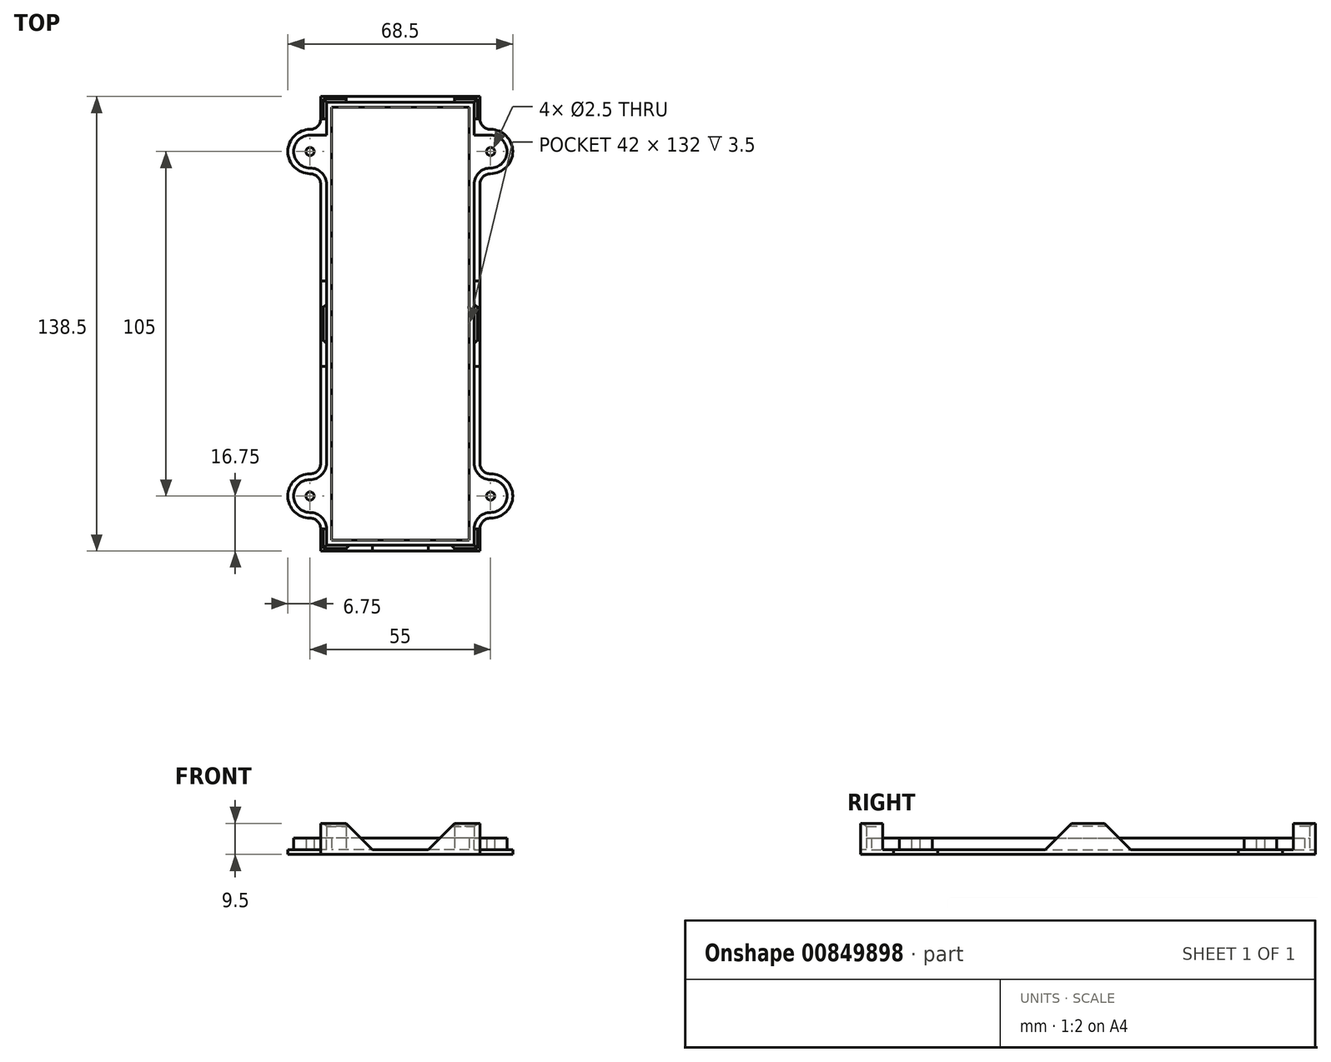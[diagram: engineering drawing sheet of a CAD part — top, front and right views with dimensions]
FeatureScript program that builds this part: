
annotation { "Feature Type Name" : "Feature", "Feature Type Description" : "" }
export const myFeature = defineFeature(function(context is Context, id is Id, definition is map)
    precondition{}
    {
        {
            var Q0;
            Q0=qCreatedBy(makeId("Top.planeOp"),FACE);
            var sketch = newSketch(context, id + "F0", { "sketchPlane" : qUnion([Q0])});
            skLineSegment(sketch, "E0.bottom", {"start": v(0, 0) * mm, "end": v(-45, 0) * mm});
            skLineSegment(sketch, "E0.top", {"start": v(0, 135) * mm, "end": v(-45, 135) * mm});
            skLineSegment(sketch, "E0.left", {"start": v(0, 0) * mm, "end": v(0, 135) * mm});
            skLineSegment(sketch, "E0.right", {"start": v(-45, 0) * mm, "end": v(-45, 135) * mm});
            skSolve(sketch);
        }
        {
            var Q0;
            Q0=qSketchRegion(id+"F0",true);
            extrude(context, id + "F1", {"entities" : qUnion([Q0]), "depth" : 40 * mm, "offsetDistance" : 25 * mm});
        }
        {
            var Q0;
            Q0=makeQuery(id+"F1.opExtrude","CAP_FACE",FACE,{"disambiguationData":[OSD([sQuery(id+"F0.wireOp",EDGE,"E0.bottom"),sQuery(id+"F0.wireOp",EDGE,"E0.top"),sQuery(id+"F0.wireOp",EDGE,"E0.left"),sQuery(id+"F0.wireOp",EDGE,"E0.right")])],"isStart":true});
            shell(context, id + "F2", {"entities" : qUnion([Q0]), "thickness" : 1.5 * mm});
        }
        {
            var Q0;
            Q0=makeQuery(id+"F1.opExtrude","CAP_FACE",FACE,{"disambiguationData":[OSD([sQuery(id+"F0.wireOp",EDGE,"E0.bottom"),sQuery(id+"F0.wireOp",EDGE,"E0.top"),sQuery(id+"F0.wireOp",EDGE,"E0.left"),sQuery(id+"F0.wireOp",EDGE,"E0.right")])],"isStart":true});
            var sketch = newSketch(context, id + "F3", { "sketchPlane" : qUnion([Q0])});
            skLineSegment(sketch, "E1.bottom", {"start": v(0, -10) * mm, "end": v(10, -10) * mm});
            skLineSegment(sketch, "E1.top", {"start": v(0, -20) * mm, "end": v(10, -20) * mm});
            skLineSegment(sketch, "E1.left", {"start": v(0, -10) * mm, "end": v(0, -20) * mm});
            skLineSegment(sketch, "E1.right", {"start": v(10, -10) * mm, "end": v(10, -20) * mm});
            skLineSegment(sketch, "E2", {"start": v(0, -67.5) * mm, "end": v(-45, -67.5) * mm, "construction": true});
            skLineSegment(sketch, "E3", {"start": v(-22.5, -135) * mm, "end": v(-22.5, 0) * mm, "construction": true});
            skLineSegment(sketch, "E4.MirrorCS", {"start": v(0, -125) * mm, "end": v(10, -125) * mm});
            skLineSegment(sketch, "E5.MirrorCS", {"start": v(0, -115) * mm, "end": v(10, -115) * mm});
            skLineSegment(sketch, "E6.MirrorCS", {"start": v(0, -125) * mm, "end": v(0, -115) * mm});
            skLineSegment(sketch, "E7.MirrorCS", {"start": v(10, -125) * mm, "end": v(10, -115) * mm});
            skLineSegment(sketch, "E8.MirrorCS", {"start": v(-55, -10) * mm, "end": v(-55, -20) * mm});
            skLineSegment(sketch, "E9.MirrorCS", {"start": v(-45, -10) * mm, "end": v(-55, -10) * mm});
            skLineSegment(sketch, "E10.MirrorCS", {"start": v(-45, -125) * mm, "end": v(-55, -125) * mm});
            skLineSegment(sketch, "E11.MirrorCS", {"start": v(-55, -125) * mm, "end": v(-55, -115) * mm});
            skLineSegment(sketch, "E12.MirrorCS", {"start": v(-45, -125) * mm, "end": v(-45, -115) * mm});
            skLineSegment(sketch, "E13.MirrorCS", {"start": v(-45, -115) * mm, "end": v(-55, -115) * mm});
            skLineSegment(sketch, "E14.MirrorCS", {"start": v(-45, -10) * mm, "end": v(-45, -20) * mm});
            skLineSegment(sketch, "E15.MirrorCS", {"start": v(-45, -20) * mm, "end": v(-55, -20) * mm});
            skLineSegment(sketch, "E16", {"start": v(5, -10) * mm, "end": v(5, -20) * mm, "construction": true});
            skCircle(sketch, "E17", {"center": v(5, -15) * mm, "radius": 1.25 * mm});
            skCircle(sketch, "E18.MirrorC", {"center": v(5, -120) * mm, "radius": 1.25 * mm});
            skCircle(sketch, "E19.MirrorC", {"center": v(-50, -120) * mm, "radius": 1.25 * mm});
            skCircle(sketch, "E20.MirrorC", {"center": v(-50, -15) * mm, "radius": 1.25 * mm});
            skSolve(sketch);
        }
        {
            var Q0;
            Q0=qSketchRegion(id+"F3",true);
            var Q1;
            Q1=makeQuery(id+"F1.opExtrude","CAP_FACE",FACE,{"disambiguationData":[OSD([sQuery(id+"F0.wireOp",EDGE,"E0.bottom"),sQuery(id+"F0.wireOp",EDGE,"E0.top"),sQuery(id+"F0.wireOp",EDGE,"E0.left"),sQuery(id+"F0.wireOp",EDGE,"E0.right")])],"isStart":false});
            extrude(context, id + "F4", {"entities" : qUnion([Q0]), "operationType" : NewBodyOperationType.ADD, "endBound" : BoundingType.UP_TO_SURFACE, "oppositeDirection" : true, "depth" : 25 * mm, "endBoundEntityFace" : qUnion([Q1]), "offsetDistance" : 25 * mm});
        }
        {
            var Q0;
            Q0=makeQuery(id+"F4.opExtrude","SWEPT_EDGE",EDGE,{"disambiguationData":[OSD([sQuery(id+"F3.wireOp",EDGE,"E1.bottom"),sQuery(id+"F3.wireOp",EDGE,"E1.right")])]});
            var Q1;
            Q1=makeQuery(id+"F4.opExtrude","SWEPT_EDGE",EDGE,{"disambiguationData":[OSD([sQuery(id+"F3.wireOp",EDGE,"E1.top"),sQuery(id+"F3.wireOp",EDGE,"E1.right")])]});
            var Q2;
            Q2=makeQuery(id+"F4.opExtrude","SWEPT_EDGE",EDGE,{"disambiguationData":[OSD([sQuery(id+"F0.wireOp",EDGE,"E0.left"),sQuery(id+"F3.wireOp",EDGE,"E1.left"),sQuery(id+"F3.wireOp",EDGE,"E1.bottom")])]});
            var Q3;
            Q3=makeQuery(id+"F4.opExtrude","SWEPT_EDGE",EDGE,{"disambiguationData":[OSD([sQuery(id+"F0.wireOp",EDGE,"E0.left"),sQuery(id+"F3.wireOp",EDGE,"E6.MirrorCS"),sQuery(id+"F3.wireOp",EDGE,"E5.MirrorCS")])]});
            var Q4;
            Q4=makeQuery(id+"F4.opExtrude","SWEPT_EDGE",EDGE,{"disambiguationData":[OSD([sQuery(id+"F3.wireOp",EDGE,"E5.MirrorCS"),sQuery(id+"F3.wireOp",EDGE,"E7.MirrorCS")])]});
            var Q5;
            Q5=makeQuery(id+"F4.opExtrude","SWEPT_EDGE",EDGE,{"disambiguationData":[OSD([sQuery(id+"F3.wireOp",EDGE,"E4.MirrorCS"),sQuery(id+"F3.wireOp",EDGE,"E7.MirrorCS")])]});
            var Q6;
            Q6=makeQuery(id+"F4.opExtrude","SWEPT_EDGE",EDGE,{"disambiguationData":[OSD([sQuery(id+"F0.wireOp",EDGE,"E0.left"),sQuery(id+"F3.wireOp",EDGE,"E1.top"),sQuery(id+"F3.wireOp",EDGE,"E1.left")])]});
            var Q7;
            Q7=makeQuery(id+"F4.opExtrude","SWEPT_EDGE",EDGE,{"disambiguationData":[OSD([sQuery(id+"F0.wireOp",EDGE,"E0.left"),sQuery(id+"F3.wireOp",EDGE,"E6.MirrorCS"),sQuery(id+"F3.wireOp",EDGE,"E4.MirrorCS")])]});
            var Q8;
            Q8=makeQuery(id+"F4.opExtrude","SWEPT_EDGE",EDGE,{"disambiguationData":[OSD([sQuery(id+"F3.wireOp",EDGE,"E10.MirrorCS"),sQuery(id+"F3.wireOp",EDGE,"E11.MirrorCS")])]});
            var Q9;
            Q9=makeQuery(id+"F4.opExtrude","SWEPT_EDGE",EDGE,{"disambiguationData":[OSD([sQuery(id+"F3.wireOp",EDGE,"E13.MirrorCS"),sQuery(id+"F3.wireOp",EDGE,"E11.MirrorCS")])]});
            var Q10;
            Q10=makeQuery(id+"F4.opExtrude","SWEPT_EDGE",EDGE,{"disambiguationData":[OSD([sQuery(id+"F0.wireOp",EDGE,"E0.right"),sQuery(id+"F3.wireOp",EDGE,"E13.MirrorCS"),sQuery(id+"F3.wireOp",EDGE,"E12.MirrorCS")])]});
            var Q11;
            Q11=makeQuery(id+"F4.opExtrude","SWEPT_EDGE",EDGE,{"disambiguationData":[OSD([sQuery(id+"F3.wireOp",EDGE,"E15.MirrorCS"),sQuery(id+"F3.wireOp",EDGE,"E8.MirrorCS")])]});
            var Q12;
            Q12=makeQuery(id+"F4.opExtrude","SWEPT_EDGE",EDGE,{"disambiguationData":[OSD([sQuery(id+"F3.wireOp",EDGE,"E9.MirrorCS"),sQuery(id+"F3.wireOp",EDGE,"E8.MirrorCS")])]});
            var Q13;
            Q13=makeQuery(id+"F4.opExtrude","SWEPT_EDGE",EDGE,{"disambiguationData":[OSD([sQuery(id+"F0.wireOp",EDGE,"E0.right"),sQuery(id+"F3.wireOp",EDGE,"E14.MirrorCS"),sQuery(id+"F3.wireOp",EDGE,"E9.MirrorCS")])]});
            var Q14;
            Q14=makeQuery(id+"F4.opExtrude","SWEPT_EDGE",EDGE,{"disambiguationData":[OSD([sQuery(id+"F0.wireOp",EDGE,"E0.right"),sQuery(id+"F3.wireOp",EDGE,"E14.MirrorCS"),sQuery(id+"F3.wireOp",EDGE,"E15.MirrorCS")])]});
            var Q15;
            Q15=makeQuery(id+"F4.opExtrude","SWEPT_EDGE",EDGE,{"disambiguationData":[OSD([sQuery(id+"F0.wireOp",EDGE,"E0.right"),sQuery(id+"F3.wireOp",EDGE,"E10.MirrorCS"),sQuery(id+"F3.wireOp",EDGE,"E12.MirrorCS")])]});
            fillet(context, id + "F5", {"entities" : qUnion([Q0, Q1, Q2, Q3, Q4, Q5, Q6, Q7, Q8, Q9, Q10, Q11, Q12, Q13, Q14, Q15]), "radius" : 5 * mm, "tangentPropagation" : true, "allowEdgeOverflow" : false});
        }
        {
            var Q0;
            {var subQ0=sQuery(id+"F0.wireOp",EDGE,"E0.right");var subQ1=sQuery(id+"F0.wireOp",EDGE,"E0.left");var subQ2=sQuery(id+"F0.wireOp",EDGE,"E0.top");var subQ3=sQuery(id+"F0.wireOp",EDGE,"E0.bottom");Q0=makeQuery(id+"FaDlpkemfFyatg3_1.boolean.opBoolean","MERGE",FACE,{"derivedFrom":[makeQuery(id+"FYj0XSdouHRkD70_1.boolean.opBoolean","MERGE",FACE,{"derivedFrom":[makeQuery(id+"F4.boolean.opBoolean","MERGE",FACE,{"derivedFrom":[makeQuery(id+"F1.opExtrude","CAP_FACE",FACE,{"disambiguationData":[OSD([subQ3,subQ2,subQ1,subQ0])],"isStart":false}),makeQuery(id+"F4.opExtrude","CAP_FACE",FACE,{"disambiguationData":[OSD([subQ3,subQ2,subQ1,subQ0]),OD(0.0)],"isStart":false}),makeQuery(id+"F4.opExtrude","CAP_FACE",FACE,{"disambiguationData":[OSD([subQ3,subQ2,subQ1,subQ0]),OD(1.0)],"isStart":false}),makeQuery(id+"F4.opExtrude","CAP_FACE",FACE,{"disambiguationData":[OSD([subQ3,subQ2,subQ1,subQ0]),OD(2.0)],"isStart":false}),makeQuery(id+"F4.opExtrude","CAP_FACE",FACE,{"disambiguationData":[OSD([subQ3,subQ2,subQ1,subQ0]),OD(3.0)],"isStart":false})]}),makeQuery(id+"FYj0XSdouHRkD70_1.opExtrude","CAP_FACE",FACE,{"disambiguationData":[OSD([sQuery(id+"F8WeWjaxWwTCFmq_1.wireOp",EDGE,"93d23473-a2ef-47fb-ade2-3e416f20a17d0.MirrorCS"),sQuery(id+"F8WeWjaxWwTCFmq_1.wireOp",EDGE,"93d23473-a2ef-47fb-ade2-3e416f20a17d3.MirrorCS"),sQuery(id+"F8WeWjaxWwTCFmq_1.wireOp",EDGE,"93d23473-a2ef-47fb-ade2-3e416f20a17d4.MirrorCS"),sQuery(id+"F8WeWjaxWwTCFmq_1.wireOp",EDGE,"93d23473-a2ef-47fb-ade2-3e416f20a17d5.MirrorCS")])],"isStart":true}),makeQuery(id+"FYj0XSdouHRkD70_1.opExtrude","CAP_FACE",FACE,{"disambiguationData":[OSD([sQuery(id+"F8WeWjaxWwTCFmq_1.wireOp",EDGE,"93d23473-a2ef-47fb-ade2-3e416f20a17d1.MirrorCS"),sQuery(id+"F8WeWjaxWwTCFmq_1.wireOp",EDGE,"93d23473-a2ef-47fb-ade2-3e416f20a17d2.MirrorCS"),sQuery(id+"F8WeWjaxWwTCFmq_1.wireOp",EDGE,"93d23473-a2ef-47fb-ade2-3e416f20a17d6.MirrorCS"),sQuery(id+"F8WeWjaxWwTCFmq_1.wireOp",EDGE,"93d23473-a2ef-47fb-ade2-3e416f20a17d7.MirrorCS")])],"isStart":true}),makeQuery(id+"FYj0XSdouHRkD70_1.opExtrude","CAP_FACE",FACE,{"disambiguationData":[OSD([sQuery(id+"F8WeWjaxWwTCFmq_1.wireOp",EDGE,"fb27c33a-4866-4415-b474-31c7e862b3b04.MirrorCS"),sQuery(id+"F8WeWjaxWwTCFmq_1.wireOp",EDGE,"fb27c33a-4866-4415-b474-31c7e862b3b05.MirrorCS"),sQuery(id+"F8WeWjaxWwTCFmq_1.wireOp",EDGE,"fb27c33a-4866-4415-b474-31c7e862b3b012.MirrorCS"),sQuery(id+"F8WeWjaxWwTCFmq_1.wireOp",EDGE,"fb27c33a-4866-4415-b474-31c7e862b3b014.MirrorCS")])],"isStart":true}),makeQuery(id+"FYj0XSdouHRkD70_1.opExtrude","CAP_FACE",FACE,{"disambiguationData":[OSD([sQuery(id+"F8WeWjaxWwTCFmq_1.wireOp",EDGE,"fb27c33a-4866-4415-b474-31c7e862b3b06.MirrorCS"),sQuery(id+"F8WeWjaxWwTCFmq_1.wireOp",EDGE,"fb27c33a-4866-4415-b474-31c7e862b3b07.MirrorCS"),sQuery(id+"F8WeWjaxWwTCFmq_1.wireOp",EDGE,"fb27c33a-4866-4415-b474-31c7e862b3b013.MirrorCS"),sQuery(id+"F8WeWjaxWwTCFmq_1.wireOp",EDGE,"fb27c33a-4866-4415-b474-31c7e862b3b015.MirrorCS")])],"isStart":true}),makeQuery(id+"FYj0XSdouHRkD70_1.opExtrude","CAP_FACE",FACE,{"disambiguationData":[OSD([sQuery(id+"F8WeWjaxWwTCFmq_1.wireOp",EDGE,"8594dad5-c960-4ccd-87cf-11f5807737a04.MirrorCS"),sQuery(id+"F8WeWjaxWwTCFmq_1.wireOp",EDGE,"8594dad5-c960-4ccd-87cf-11f5807737a05.MirrorCS"),sQuery(id+"F8WeWjaxWwTCFmq_1.wireOp",EDGE,"8594dad5-c960-4ccd-87cf-11f5807737a013.MirrorCS"),sQuery(id+"F8WeWjaxWwTCFmq_1.wireOp",EDGE,"8594dad5-c960-4ccd-87cf-11f5807737a015.MirrorCS")])],"isStart":true}),makeQuery(id+"FYj0XSdouHRkD70_1.opExtrude","CAP_FACE",FACE,{"disambiguationData":[OSD([sQuery(id+"F8WeWjaxWwTCFmq_1.wireOp",EDGE,"8594dad5-c960-4ccd-87cf-11f5807737a06.MirrorCS"),sQuery(id+"F8WeWjaxWwTCFmq_1.wireOp",EDGE,"8594dad5-c960-4ccd-87cf-11f5807737a07.MirrorCS"),sQuery(id+"F8WeWjaxWwTCFmq_1.wireOp",EDGE,"8594dad5-c960-4ccd-87cf-11f5807737a012.MirrorCS"),sQuery(id+"F8WeWjaxWwTCFmq_1.wireOp",EDGE,"8594dad5-c960-4ccd-87cf-11f5807737a014.MirrorCS")])],"isStart":true}),makeQuery(id+"FYj0XSdouHRkD70_1.opExtrude","CAP_FACE",FACE,{"disambiguationData":[OSD([sQuery(id+"F8WeWjaxWwTCFmq_1.wireOp",EDGE,"8594dad5-c960-4ccd-87cf-11f5807737a024.MirrorCS"),sQuery(id+"F8WeWjaxWwTCFmq_1.wireOp",EDGE,"8594dad5-c960-4ccd-87cf-11f5807737a026.MirrorCS"),sQuery(id+"F8WeWjaxWwTCFmq_1.wireOp",EDGE,"8594dad5-c960-4ccd-87cf-11f5807737a037.MirrorCS"),sQuery(id+"F8WeWjaxWwTCFmq_1.wireOp",EDGE,"8594dad5-c960-4ccd-87cf-11f5807737a039.MirrorCS")])],"isStart":true}),makeQuery(id+"FYj0XSdouHRkD70_1.opExtrude","CAP_FACE",FACE,{"disambiguationData":[OSD([sQuery(id+"F8WeWjaxWwTCFmq_1.wireOp",EDGE,"8594dad5-c960-4ccd-87cf-11f5807737a025.MirrorCS"),sQuery(id+"F8WeWjaxWwTCFmq_1.wireOp",EDGE,"8594dad5-c960-4ccd-87cf-11f5807737a027.MirrorCS"),sQuery(id+"F8WeWjaxWwTCFmq_1.wireOp",EDGE,"8594dad5-c960-4ccd-87cf-11f5807737a036.MirrorCS"),sQuery(id+"F8WeWjaxWwTCFmq_1.wireOp",EDGE,"8594dad5-c960-4ccd-87cf-11f5807737a038.MirrorCS")])],"isStart":true})]}),makeQuery(id+"FaDlpkemfFyatg3_1.opExtrude","CAP_FACE",FACE,{"disambiguationData":[OSD([sQuery(id+"FW0xXjJy58C57Ev_1.wireOp",EDGE,"CDe6ZgkD-YJ72-r8PF-ca2P-he8DJ2cccsRQ.bottom"),sQuery(id+"FW0xXjJy58C57Ev_1.wireOp",EDGE,"CDe6ZgkD-YJ72-r8PF-ca2P-he8DJ2cccsRQ.top"),sQuery(id+"FW0xXjJy58C57Ev_1.wireOp",EDGE,"CDe6ZgkD-YJ72-r8PF-ca2P-he8DJ2cccsRQ.left"),sQuery(id+"FW0xXjJy58C57Ev_1.wireOp",EDGE,"CDe6ZgkD-YJ72-r8PF-ca2P-he8DJ2cccsRQ.right")])],"isStart":true}),makeQuery(id+"FaDlpkemfFyatg3_1.opExtrude","CAP_FACE",FACE,{"disambiguationData":[OSD([sQuery(id+"FW0xXjJy58C57Ev_1.wireOp",EDGE,"HdfrrGbN-Y0IQ-oc1Z-EoYa-jZvDq0JLBEhN.bottom"),sQuery(id+"FW0xXjJy58C57Ev_1.wireOp",EDGE,"HdfrrGbN-Y0IQ-oc1Z-EoYa-jZvDq0JLBEhN.top"),sQuery(id+"FW0xXjJy58C57Ev_1.wireOp",EDGE,"HdfrrGbN-Y0IQ-oc1Z-EoYa-jZvDq0JLBEhN.left"),sQuery(id+"FW0xXjJy58C57Ev_1.wireOp",EDGE,"HdfrrGbN-Y0IQ-oc1Z-EoYa-jZvDq0JLBEhN.right")])],"isStart":true})]});}
            var sketch = newSketch(context, id + "F6", { "sketchPlane" : qUnion([Q0])});
            skLineSegment(sketch, "E21.bottom", {"start": v(-55, 0) * mm, "end": v(10, 0) * mm});
            skLineSegment(sketch, "E21.top", {"start": v(-55, 135) * mm, "end": v(10, 135) * mm});
            skLineSegment(sketch, "E21.left", {"start": v(-55, 0) * mm, "end": v(-55, 135) * mm});
            skLineSegment(sketch, "E21.right", {"start": v(10, 0) * mm, "end": v(10, 135) * mm});
            skSolve(sketch);
        }
        {
            var Q0;
            Q0 = qSketchRegion(id + "F6", true);
            var Q1;
            {var subQ0=sQuery(id+"F3.wireOp",EDGE,"E15.MirrorCS");var subQ1=sQuery(id+"F3.wireOp",EDGE,"E14.MirrorCS");var subQ2=sQuery(id+"F0.wireOp",EDGE,"E0.right");var subQ3=sQuery(id+"F3.wireOp",EDGE,"E20.MirrorC");var subQ4=sQuery(id+"F3.wireOp",EDGE,"E9.MirrorCS");var subQ5=sQuery(id+"F3.wireOp",EDGE,"E19.MirrorC");var subQ6=sQuery(id+"F3.wireOp",EDGE,"E18.MirrorC");var subQ7=sQuery(id+"F3.wireOp",EDGE,"E12.MirrorCS");var subQ8=sQuery(id+"F3.wireOp",EDGE,"E10.MirrorCS");var subQ9=sQuery(id+"F3.wireOp",EDGE,"E17");var subQ10=sQuery(id+"F3.wireOp",EDGE,"E13.MirrorCS");var subQ11=sQuery(id+"F3.wireOp",EDGE,"E4.MirrorCS");var subQ12=sQuery(id+"F3.wireOp",EDGE,"E6.MirrorCS");var subQ13=sQuery(id+"F0.wireOp",EDGE,"E0.left");var subQ14=sQuery(id+"F3.wireOp",EDGE,"E5.MirrorCS");var subQ15=sQuery(id+"F3.wireOp",EDGE,"E8.MirrorCS");var subQ16=sQuery(id+"F3.wireOp",EDGE,"E11.MirrorCS");var subQ17=sQuery(id+"F3.wireOp",EDGE,"E1.right");var subQ18=sQuery(id+"F3.wireOp",EDGE,"E1.bottom");var subQ19=sQuery(id+"F3.wireOp",EDGE,"E7.MirrorCS");var subQ20=sQuery(id+"F3.wireOp",EDGE,"E1.left");var subQ21=sQuery(id+"F3.wireOp",EDGE,"E1.top");var subQ22=sQuery(id+"F0.wireOp",EDGE,"E0.top");var subQ23=sQuery(id+"F0.wireOp",EDGE,"E0.bottom");Q1=makeQuery(id+"FUpLiOi44v6v76Y_1.boolean.opBoolean","SPLIT",FACE,{"disambiguationData":[TD([makeQuery(id+"F1.opExtrude","SWEPT_FACE",FACE,{"disambiguationData":[OSD([subQ22])]})])],"derivedFrom":makeQuery(id+"FYj0XSdouHRkD70_1.boolean.opBoolean","MERGE",FACE,{"derivedFrom":[makeQuery(id+"F4.boolean.opBoolean","MERGE",FACE,{"derivedFrom":[makeQuery(id+"F1.opExtrude","CAP_FACE",FACE,{"disambiguationData":[OSD([subQ23,subQ22,subQ13,subQ2])],"isStart":true}),makeQuery(id+"F4.opExtrude","CAP_FACE",FACE,{"disambiguationData":[OSD([subQ21,subQ20,subQ18,subQ17,subQ9])],"isStart":true}),makeQuery(id+"F4.opExtrude","CAP_FACE",FACE,{"disambiguationData":[OSD([subQ12,subQ11,subQ14,subQ19,subQ6])],"isStart":true}),makeQuery(id+"F4.opExtrude","CAP_FACE",FACE,{"disambiguationData":[OSD([subQ10,subQ8,subQ16,subQ7,subQ5])],"isStart":true}),makeQuery(id+"F4.opExtrude","CAP_FACE",FACE,{"disambiguationData":[OSD([subQ1,subQ4,subQ0,subQ15,subQ3])],"isStart":true})]}),makeQuery(id+"FYj0XSdouHRkD70_1.opExtrude","CAP_FACE",FACE,{"disambiguationData":[OSD([subQ23,subQ22,subQ13,subQ2,subQ21,subQ20,subQ12,subQ11,subQ14,subQ19,subQ18,subQ17,subQ10,subQ8,subQ1,subQ4,subQ16,subQ0,subQ7,subQ15,subQ9,subQ6,subQ5,subQ3]),OD(0.0)],"isStart":false}),makeQuery(id+"FYj0XSdouHRkD70_1.opExtrude","CAP_FACE",FACE,{"disambiguationData":[OSD([subQ23,subQ22,subQ13,subQ2,subQ21,subQ20,subQ12,subQ11,subQ14,subQ19,subQ18,subQ17,subQ10,subQ8,subQ1,subQ4,subQ16,subQ0,subQ7,subQ15,subQ9,subQ6,subQ5,subQ3]),OD(1.0)],"isStart":false}),makeQuery(id+"FYj0XSdouHRkD70_1.opExtrude","CAP_FACE",FACE,{"disambiguationData":[OSD([subQ23,subQ22,subQ13,subQ2,subQ21,subQ20,subQ12,subQ11,subQ14,subQ19,subQ18,subQ17,subQ10,subQ8,subQ1,subQ4,subQ16,subQ0,subQ7,subQ15,subQ9,subQ6,subQ5,subQ3]),OD(2.0)],"isStart":false}),makeQuery(id+"FYj0XSdouHRkD70_1.opExtrude","CAP_FACE",FACE,{"disambiguationData":[OSD([subQ23,subQ22,subQ13,subQ2,subQ21,subQ20,subQ12,subQ11,subQ14,subQ19,subQ18,subQ17,subQ10,subQ8,subQ1,subQ4,subQ16,subQ0,subQ7,subQ15,subQ9,subQ6,subQ5,subQ3]),OD(3.0)],"isStart":false}),makeQuery(id+"FYj0XSdouHRkD70_1.opExtrude","CAP_FACE",FACE,{"disambiguationData":[OSD([subQ23,subQ22,subQ13,subQ2,subQ21,subQ20,subQ12,subQ11,subQ14,subQ19,subQ18,subQ17,subQ10,subQ8,subQ1,subQ4,subQ16,subQ0,subQ7,subQ15,subQ9,subQ6,subQ5,subQ3]),OD(4.0)],"isStart":false}),makeQuery(id+"FYj0XSdouHRkD70_1.opExtrude","CAP_FACE",FACE,{"disambiguationData":[OSD([subQ23,subQ22,subQ13,subQ2,subQ21,subQ20,subQ12,subQ11,subQ14,subQ19,subQ18,subQ17,subQ10,subQ8,subQ1,subQ4,subQ16,subQ0,subQ7,subQ15,subQ9,subQ6,subQ5,subQ3]),OD(5.0)],"isStart":false}),makeQuery(id+"FYj0XSdouHRkD70_1.opExtrude","CAP_FACE",FACE,{"disambiguationData":[OSD([subQ23,subQ22,subQ13,subQ2,subQ21,subQ20,subQ12,subQ11,subQ14,subQ19,subQ18,subQ17,subQ10,subQ8,subQ1,subQ4,subQ16,subQ0,subQ7,subQ15,subQ9,subQ6,subQ5,subQ3]),OD(6.0)],"isStart":false}),makeQuery(id+"FYj0XSdouHRkD70_1.opExtrude","CAP_FACE",FACE,{"disambiguationData":[OSD([subQ23,subQ22,subQ13,subQ2,subQ21,subQ20,subQ12,subQ11,subQ14,subQ19,subQ18,subQ17,subQ10,subQ8,subQ1,subQ4,subQ16,subQ0,subQ7,subQ15,subQ9,subQ6,subQ5,subQ3]),OD(7.0)],"isStart":false})]})});}
            extrude(context, id + "F7", {"entities" : qUnion([Q0]), "operationType" : NewBodyOperationType.REMOVE, "endBound" : BoundingType.UP_TO_SURFACE, "oppositeDirection" : true, "depth" : 25 * mm, "endBoundEntityFace" : qUnion([Q1]), "hasOffset" : true, "offsetDistance" : 3.5 * mm});
        }
        {
            var Q0;
            {var subQ0=sQuery(id+"F3.wireOp",EDGE,"E20.MirrorC");var subQ1=sQuery(id+"F3.wireOp",EDGE,"E19.MirrorC");var subQ2=sQuery(id+"F3.wireOp",EDGE,"E18.MirrorC");var subQ3=sQuery(id+"F3.wireOp",EDGE,"E17");var subQ4=sQuery(id+"F3.wireOp",EDGE,"E8.MirrorCS");var subQ5=sQuery(id+"F3.wireOp",EDGE,"E12.MirrorCS");var subQ6=sQuery(id+"F3.wireOp",EDGE,"E15.MirrorCS");var subQ7=sQuery(id+"F3.wireOp",EDGE,"E11.MirrorCS");var subQ8=sQuery(id+"F3.wireOp",EDGE,"E9.MirrorCS");var subQ9=sQuery(id+"F3.wireOp",EDGE,"E14.MirrorCS");var subQ10=sQuery(id+"F3.wireOp",EDGE,"E10.MirrorCS");var subQ11=sQuery(id+"F3.wireOp",EDGE,"E13.MirrorCS");var subQ12=sQuery(id+"F3.wireOp",EDGE,"E1.right");var subQ13=sQuery(id+"F3.wireOp",EDGE,"E1.bottom");var subQ14=sQuery(id+"F3.wireOp",EDGE,"E7.MirrorCS");var subQ15=sQuery(id+"F3.wireOp",EDGE,"E5.MirrorCS");var subQ16=sQuery(id+"F3.wireOp",EDGE,"E4.MirrorCS");var subQ17=sQuery(id+"F3.wireOp",EDGE,"E6.MirrorCS");var subQ18=sQuery(id+"F3.wireOp",EDGE,"E1.left");var subQ19=sQuery(id+"F3.wireOp",EDGE,"E1.top");var subQ20=sQuery(id+"F0.wireOp",EDGE,"E0.right");var subQ21=sQuery(id+"F0.wireOp",EDGE,"E0.left");var subQ22=sQuery(id+"F0.wireOp",EDGE,"E0.top");var subQ23=sQuery(id+"F0.wireOp",EDGE,"E0.bottom");Q0=makeQuery(id+"FYj0XSdouHRkD70_1.boolean.opBoolean","MERGE",FACE,{"derivedFrom":[makeQuery(id+"F4.boolean.opBoolean","MERGE",FACE,{"derivedFrom":[makeQuery(id+"F1.opExtrude","CAP_FACE",FACE,{"disambiguationData":[OSD([subQ23,subQ22,subQ21,subQ20])],"isStart":true}),makeQuery(id+"F4.opExtrude","CAP_FACE",FACE,{"disambiguationData":[OSD([subQ19,subQ18,subQ13,subQ12,subQ3])],"isStart":true}),makeQuery(id+"F4.opExtrude","CAP_FACE",FACE,{"disambiguationData":[OSD([subQ17,subQ16,subQ15,subQ14,subQ2])],"isStart":true}),makeQuery(id+"F4.opExtrude","CAP_FACE",FACE,{"disambiguationData":[OSD([subQ11,subQ10,subQ7,subQ5,subQ1])],"isStart":true}),makeQuery(id+"F4.opExtrude","CAP_FACE",FACE,{"disambiguationData":[OSD([subQ9,subQ8,subQ6,subQ4,subQ0])],"isStart":true})]}),makeQuery(id+"FYj0XSdouHRkD70_1.opExtrude","CAP_FACE",FACE,{"disambiguationData":[OSD([subQ23,subQ22,subQ21,subQ20,subQ19,subQ18,subQ17,subQ16,subQ15,subQ14,subQ13,subQ12,subQ11,subQ10,subQ9,subQ8,subQ7,subQ6,subQ5,subQ4,subQ3,subQ2,subQ1,subQ0]),OD(0.0)],"isStart":false}),makeQuery(id+"FYj0XSdouHRkD70_1.opExtrude","CAP_FACE",FACE,{"disambiguationData":[OSD([subQ23,subQ22,subQ21,subQ20,subQ19,subQ18,subQ17,subQ16,subQ15,subQ14,subQ13,subQ12,subQ11,subQ10,subQ9,subQ8,subQ7,subQ6,subQ5,subQ4,subQ3,subQ2,subQ1,subQ0]),OD(1.0)],"isStart":false}),makeQuery(id+"FYj0XSdouHRkD70_1.opExtrude","CAP_FACE",FACE,{"disambiguationData":[OSD([subQ23,subQ22,subQ21,subQ20,subQ19,subQ18,subQ17,subQ16,subQ15,subQ14,subQ13,subQ12,subQ11,subQ10,subQ9,subQ8,subQ7,subQ6,subQ5,subQ4,subQ3,subQ2,subQ1,subQ0]),OD(2.0)],"isStart":false}),makeQuery(id+"FYj0XSdouHRkD70_1.opExtrude","CAP_FACE",FACE,{"disambiguationData":[OSD([subQ23,subQ22,subQ21,subQ20,subQ19,subQ18,subQ17,subQ16,subQ15,subQ14,subQ13,subQ12,subQ11,subQ10,subQ9,subQ8,subQ7,subQ6,subQ5,subQ4,subQ3,subQ2,subQ1,subQ0]),OD(3.0)],"isStart":false}),makeQuery(id+"FYj0XSdouHRkD70_1.opExtrude","CAP_FACE",FACE,{"disambiguationData":[OSD([subQ23,subQ22,subQ21,subQ20,subQ19,subQ18,subQ17,subQ16,subQ15,subQ14,subQ13,subQ12,subQ11,subQ10,subQ9,subQ8,subQ7,subQ6,subQ5,subQ4,subQ3,subQ2,subQ1,subQ0]),OD(4.0)],"isStart":false}),makeQuery(id+"FYj0XSdouHRkD70_1.opExtrude","CAP_FACE",FACE,{"disambiguationData":[OSD([subQ23,subQ22,subQ21,subQ20,subQ19,subQ18,subQ17,subQ16,subQ15,subQ14,subQ13,subQ12,subQ11,subQ10,subQ9,subQ8,subQ7,subQ6,subQ5,subQ4,subQ3,subQ2,subQ1,subQ0]),OD(5.0)],"isStart":false}),makeQuery(id+"FYj0XSdouHRkD70_1.opExtrude","CAP_FACE",FACE,{"disambiguationData":[OSD([subQ23,subQ22,subQ21,subQ20,subQ19,subQ18,subQ17,subQ16,subQ15,subQ14,subQ13,subQ12,subQ11,subQ10,subQ9,subQ8,subQ7,subQ6,subQ5,subQ4,subQ3,subQ2,subQ1,subQ0]),OD(6.0)],"isStart":false}),makeQuery(id+"FYj0XSdouHRkD70_1.opExtrude","CAP_FACE",FACE,{"disambiguationData":[OSD([subQ23,subQ22,subQ21,subQ20,subQ19,subQ18,subQ17,subQ16,subQ15,subQ14,subQ13,subQ12,subQ11,subQ10,subQ9,subQ8,subQ7,subQ6,subQ5,subQ4,subQ3,subQ2,subQ1,subQ0]),OD(7.0)],"isStart":false})]});}
            var sketch = newSketch(context, id + "F8", { "sketchPlane" : qUnion([Q0])});
            skLineSegment(sketch, "E22.0", {"start": v(-46.75, 1.75) * mm, "end": v(-46.75, -5) * mm});
            skLineSegment(sketch, "E22.1", {"start": v(1.75, 1.75) * mm, "end": v(-46.75, 1.75) * mm});
            skLineSegment(sketch, "E22.2", {"start": v(1.75, -5) * mm, "end": v(1.75, 1.75) * mm});
            skArc(sketch, "E22.3", {"start": v(5, -8.25) * mm, "mid": v(2.7, -7.3) * mm, "end": v(1.75, -5) * mm});
            skLineSegment(sketch, "E22.4", {"start": v(5, -8.25) * mm, "end": v(5, -8.25) * mm});
            skArc(sketch, "E22.6", {"start": v(5, -21.75) * mm, "mid": v(11.75, -15) * mm, "end": v(5, -8.25) * mm});
            skLineSegment(sketch, "E22.8", {"start": v(5, -21.75) * mm, "end": v(5, -21.75) * mm});
            skArc(sketch, "E22.9", {"start": v(1.75, -25) * mm, "mid": v(2.7, -22.7) * mm, "end": v(5, -21.75) * mm});
            skLineSegment(sketch, "E22.10", {"start": v(1.75, -110) * mm, "end": v(1.75, -25) * mm});
            skArc(sketch, "E22.11", {"start": v(-46.75, -5) * mm, "mid": v(-47.7, -7.3) * mm, "end": v(-50, -8.25) * mm});
            skArc(sketch, "E22.12", {"start": v(5, -113.25) * mm, "mid": v(2.7, -112.3) * mm, "end": v(1.75, -110) * mm});
            skLineSegment(sketch, "E22.13", {"start": v(5, -113.25) * mm, "end": v(5, -113.25) * mm});
            skLineSegment(sketch, "E22.15", {"start": v(-50, -113.25) * mm, "end": v(-50, -113.25) * mm});
            skArc(sketch, "E22.16", {"start": v(-46.75, -110) * mm, "mid": v(-47.7, -112.3) * mm, "end": v(-50, -113.25) * mm});
            skLineSegment(sketch, "E22.17", {"start": v(-46.75, -25) * mm, "end": v(-46.75, -110) * mm});
            skArc(sketch, "E22.18", {"start": v(-50, -21.75) * mm, "mid": v(-47.7, -22.7) * mm, "end": v(-46.75, -25) * mm});
            skLineSegment(sketch, "E22.19", {"start": v(-50, -21.75) * mm, "end": v(-50, -21.75) * mm});
            skLineSegment(sketch, "E22.20", {"start": v(-50, -8.25) * mm, "end": v(-50, -8.25) * mm});
            skArc(sketch, "E22.22", {"start": v(-50, -8.25) * mm, "mid": v(-56.75, -15) * mm, "end": v(-50, -21.75) * mm});
            skArc(sketch, "E22.24", {"start": v(-50, -113.25) * mm, "mid": v(-56.75, -120) * mm, "end": v(-50, -126.75) * mm});
            skLineSegment(sketch, "E22.26", {"start": v(-50, -126.75) * mm, "end": v(-50, -126.75) * mm});
            skArc(sketch, "E22.27", {"start": v(-50, -126.75) * mm, "mid": v(-47.7, -127.7) * mm, "end": v(-46.75, -130) * mm});
            skLineSegment(sketch, "E22.28", {"start": v(-46.75, -130) * mm, "end": v(-46.75, -136.75) * mm});
            skLineSegment(sketch, "E22.29", {"start": v(-46.75, -136.75) * mm, "end": v(1.75, -136.75) * mm});
            skLineSegment(sketch, "E22.30", {"start": v(1.75, -136.75) * mm, "end": v(1.75, -130) * mm});
            skArc(sketch, "E22.31", {"start": v(1.75, -130) * mm, "mid": v(2.7, -127.7) * mm, "end": v(5, -126.75) * mm});
            skLineSegment(sketch, "E22.32", {"start": v(5, -126.75) * mm, "end": v(5, -126.75) * mm});
            skArc(sketch, "E22.34", {"start": v(5, -126.75) * mm, "mid": v(11.75, -120) * mm, "end": v(5, -113.25) * mm});
            skCircle(sketch, "E23.0", {"center": v(5, -120) * mm, "radius": 1.25 * mm});
            skCircle(sketch, "E24.0", {"center": v(-50, -120) * mm, "radius": 1.25 * mm});
            skCircle(sketch, "E25.0", {"center": v(5, -15) * mm, "radius": 1.25 * mm});
            skCircle(sketch, "E26.0", {"center": v(-50, -15) * mm, "radius": 1.25 * mm});
            skSolve(sketch);
        }
        {
            var Q0;
            Q0 = qSketchRegion(id + "F8", true);
            extrude(context, id + "F9", {"entities" : qUnion([Q0]), "operationType" : NewBodyOperationType.ADD, "depth" : 1.5 * mm, "offsetDistance" : 25 * mm});
        }
        {
            var Q0;
            {var subQ0=sQuery(id+"F8.wireOp",EDGE,"E22.0");var subQ2=sQuery(id+"F8.wireOp",EDGE,"E22.4");var subQ3=sQuery(id+"F8.wireOp",EDGE,"E22.3");var subQ4=sQuery(id+"F8.wireOp",EDGE,"E22.2");var subQ7=sQuery(id+"F8.wireOp",EDGE,"E22.34");var subQ9=sQuery(id+"F8.wireOp",EDGE,"E22.33");var subQ10=sQuery(id+"F8.wireOp",EDGE,"E22.5");var subQ11=sQuery(id+"F8.wireOp",EDGE,"E22.29");var subQ13=sQuery(id+"F8.wireOp",EDGE,"E22.32");var subQ14=sQuery(id+"F8.wireOp",EDGE,"E22.1");var subQ16=sQuery(id+"F8.wireOp",EDGE,"E22.30");var subQ18=sQuery(id+"F8.wireOp",EDGE,"E22.31");var subQ20=sQuery(id+"F8.wireOp",EDGE,"E22.35");var subQ23=sQuery(id+"F8.wireOp",EDGE,"E22.6");var subQ24=sQuery(id+"F8.wireOp",EDGE,"E22.7");var subQ25=sQuery(id+"F8.wireOp",EDGE,"E22.8");var subQ26=sQuery(id+"F8.wireOp",EDGE,"E22.9");var subQ27=sQuery(id+"F8.wireOp",EDGE,"E22.10");var subQ28=sQuery(id+"F8.wireOp",EDGE,"E22.11");var subQ29=sQuery(id+"F8.wireOp",EDGE,"E22.12");var subQ30=sQuery(id+"F8.wireOp",EDGE,"E22.13");var subQ31=sQuery(id+"F8.wireOp",EDGE,"E22.14");var subQ32=sQuery(id+"F8.wireOp",EDGE,"E22.15");var subQ33=sQuery(id+"F8.wireOp",EDGE,"E22.16");var subQ34=sQuery(id+"F8.wireOp",EDGE,"E22.17");var subQ35=sQuery(id+"F8.wireOp",EDGE,"E22.18");var subQ36=sQuery(id+"F8.wireOp",EDGE,"E22.19");var subQ37=sQuery(id+"F8.wireOp",EDGE,"E22.20");var subQ38=sQuery(id+"F8.wireOp",EDGE,"E22.21");var subQ39=sQuery(id+"F8.wireOp",EDGE,"E22.22");var subQ40=sQuery(id+"F8.wireOp",EDGE,"E22.23");var subQ41=sQuery(id+"F8.wireOp",EDGE,"E22.24");var subQ42=sQuery(id+"F8.wireOp",EDGE,"E22.25");var subQ43=sQuery(id+"F8.wireOp",EDGE,"E22.26");var subQ44=sQuery(id+"F8.wireOp",EDGE,"E22.27");var subQ45=sQuery(id+"F8.wireOp",EDGE,"E22.28");Q0=makeQuery(id+"F9.boolean.opBoolean","SPLIT",FACE,{"disambiguationData":[TD([makeQuery(id+"F1.opExtrude","SWEPT_FACE",FACE,{"disambiguationData":[OSD([sQuery(id+"F0.wireOp",EDGE,"E0.bottom")])]})])],"derivedFrom":makeQuery(id+"F9.opExtrude","CAP_FACE",FACE,{"disambiguationData":[OSD([subQ0,subQ14,subQ4,subQ3,subQ2,subQ10,subQ23,subQ24,subQ25,subQ26,subQ27,subQ28,subQ29,subQ30,subQ31,subQ32,subQ33,subQ34,subQ35,subQ36,subQ37,subQ38,subQ39,subQ40,subQ41,subQ42,subQ43,subQ44,subQ45,subQ11,subQ16,subQ18,subQ13,subQ9,subQ7,subQ20,sQuery(id+"F8.wireOp",EDGE,"E23.0"),sQuery(id+"F8.wireOp",EDGE,"E24.0"),sQuery(id+"F8.wireOp",EDGE,"E25.0"),sQuery(id+"F8.wireOp",EDGE,"E26.0")])],"isStart":true})});}
            var sketch = newSketch(context, id + "F10", { "sketchPlane" : qUnion([Q0])});
            skLineSegment(sketch, "E27", {"start": v(-22.5, -1.75) * mm, "end": v(-22.5, 136.75) * mm, "construction": true});
            skLineSegment(sketch, "E28", {"start": v(-46.75, 67.5) * mm, "end": v(1.75, 67.5) * mm, "construction": true});
            skLineSegment(sketch, "E29", {"start": v(-46.75, 136.75) * mm, "end": v(-46.75, 130) * mm});
            skLineSegment(sketch, "E30", {"start": v(-46.75, 130) * mm, "end": v(-45, 130) * mm});
            skLineSegment(sketch, "E31", {"start": v(-45, 130) * mm, "end": v(-45, 135) * mm});
            skLineSegment(sketch, "E32", {"start": v(-45, 135) * mm, "end": v(-39, 135) * mm});
            skLineSegment(sketch, "E33", {"start": v(-39, 135) * mm, "end": v(-39, 136.75) * mm});
            skLineSegment(sketch, "E34", {"start": v(-39, 136.75) * mm, "end": v(-46.75, 136.75) * mm});
            skLineSegment(sketch, "E35.MirrorCS", {"start": v(-6, 135) * mm, "end": v(-6, 136.75) * mm});
            skLineSegment(sketch, "E36.MirrorCS", {"start": v(1.75, 130) * mm, "end": v(0, 130) * mm});
            skLineSegment(sketch, "E37.MirrorCS", {"start": v(0, 130) * mm, "end": v(0, 135) * mm});
            skLineSegment(sketch, "E38.MirrorCS", {"start": v(1.75, 136.75) * mm, "end": v(1.75, 130) * mm});
            skLineSegment(sketch, "E39.MirrorCS", {"start": v(-6, 136.75) * mm, "end": v(1.75, 136.75) * mm});
            skLineSegment(sketch, "E40.MirrorCS", {"start": v(0, 135) * mm, "end": v(-6, 135) * mm});
            skLineSegment(sketch, "E41.MirrorCS", {"start": v(-6, 0) * mm, "end": v(-6, -1.75) * mm});
            skLineSegment(sketch, "E42.MirrorCS", {"start": v(1.75, 5) * mm, "end": v(0, 5) * mm});
            skLineSegment(sketch, "E43.MirrorCS", {"start": v(-6, -1.75) * mm, "end": v(1.75, -1.75) * mm});
            skLineSegment(sketch, "E44.MirrorCS", {"start": v(0, 5) * mm, "end": v(0, 0) * mm});
            skLineSegment(sketch, "E45.MirrorCS", {"start": v(0, 0) * mm, "end": v(-6, 0) * mm});
            skLineSegment(sketch, "E46.MirrorCS", {"start": v(1.75, -1.75) * mm, "end": v(1.75, 5) * mm});
            skLineSegment(sketch, "E47.MirrorCS", {"start": v(-46.75, 5) * mm, "end": v(-45, 5) * mm});
            skLineSegment(sketch, "E48.MirrorCS", {"start": v(-45, 5) * mm, "end": v(-45, 0) * mm});
            skLineSegment(sketch, "E49.MirrorCS", {"start": v(-39, 0) * mm, "end": v(-39, -1.75) * mm});
            skLineSegment(sketch, "E50.MirrorCS", {"start": v(-45, 0) * mm, "end": v(-39, 0) * mm});
            skLineSegment(sketch, "E51.MirrorCS", {"start": v(-46.75, -1.75) * mm, "end": v(-46.75, 5) * mm});
            skLineSegment(sketch, "E52.MirrorCS", {"start": v(-39, -1.75) * mm, "end": v(-46.75, -1.75) * mm});
            skLineSegment(sketch, "E53.bottom", {"start": v(-46.75, 72.5) * mm, "end": v(-45, 72.5) * mm});
            skLineSegment(sketch, "E53.top", {"start": v(-46.75, 62.5) * mm, "end": v(-45, 62.5) * mm});
            skLineSegment(sketch, "E53.left", {"start": v(-46.75, 72.5) * mm, "end": v(-46.75, 62.5) * mm});
            skLineSegment(sketch, "E53.right", {"start": v(-45, 72.5) * mm, "end": v(-45, 62.5) * mm});
            skLineSegment(sketch, "E54.MirrorCS", {"start": v(1.75, 72.5) * mm, "end": v(0, 72.5) * mm});
            skLineSegment(sketch, "E55.MirrorCS", {"start": v(1.75, 62.5) * mm, "end": v(0, 62.5) * mm});
            skLineSegment(sketch, "E56.MirrorCS", {"start": v(1.75, 72.5) * mm, "end": v(1.75, 62.5) * mm});
            skLineSegment(sketch, "E57.MirrorCS", {"start": v(0, 72.5) * mm, "end": v(0, 62.5) * mm});
            skSolve(sketch);
        }
        {
            var Q0;
            Q0 = qSketchRegion(id + "F10", true);
            extrude(context, id + "F11", {"entities" : qUnion([Q0]), "operationType" : NewBodyOperationType.ADD, "depth" : 8 * mm, "offsetDistance" : 25 * mm});
        }
        {
            var Q0;
            Q0=makeQuery(id+"F11.opExtrude","CAP_EDGE",EDGE,{"disambiguationData":[OSD([sQuery(id+"F10.wireOp",EDGE,"E53.right")])],"isStart":false});
            var Q1;
            Q1=makeQuery(id+"F11.opExtrude","CAP_EDGE",EDGE,{"disambiguationData":[OSD([sQuery(id+"F10.wireOp",EDGE,"E48.MirrorCS")])],"isStart":false});
            var Q2;
            Q2=makeQuery(id+"F11.opExtrude","CAP_EDGE",EDGE,{"disambiguationData":[OSD([sQuery(id+"F10.wireOp",EDGE,"E50.MirrorCS")])],"isStart":false});
            var Q3;
            Q3=makeQuery(id+"F11.opExtrude","CAP_EDGE",EDGE,{"disambiguationData":[OSD([sQuery(id+"F10.wireOp",EDGE,"E45.MirrorCS")])],"isStart":false});
            var Q4;
            Q4=makeQuery(id+"F11.opExtrude","CAP_EDGE",EDGE,{"disambiguationData":[OSD([sQuery(id+"F10.wireOp",EDGE,"E44.MirrorCS")])],"isStart":false});
            var Q5;
            Q5=makeQuery(id+"F11.opExtrude","CAP_EDGE",EDGE,{"disambiguationData":[OSD([sQuery(id+"F10.wireOp",EDGE,"E57.MirrorCS")])],"isStart":false});
            var Q6;
            Q6=makeQuery(id+"F11.opExtrude","CAP_EDGE",EDGE,{"disambiguationData":[OSD([sQuery(id+"F10.wireOp",EDGE,"E31")])],"isStart":false});
            var Q7;
            Q7=makeQuery(id+"F11.opExtrude","CAP_EDGE",EDGE,{"disambiguationData":[OSD([sQuery(id+"F10.wireOp",EDGE,"E32")])],"isStart":false});
            var Q8;
            Q8=makeQuery(id+"F11.opExtrude","CAP_EDGE",EDGE,{"disambiguationData":[OSD([sQuery(id+"F10.wireOp",EDGE,"E37.MirrorCS")])],"isStart":false});
            var Q9;
            Q9=makeQuery(id+"F11.opExtrude","CAP_EDGE",EDGE,{"disambiguationData":[OSD([sQuery(id+"F10.wireOp",EDGE,"E40.MirrorCS")])],"isStart":false});
            chamfer(context, id + "F12", {"entities" : qUnion([Q0, Q1, Q2, Q3, Q4, Q5, Q6, Q7, Q8, Q9]), "width" : 1 * mm, "tangentPropagation" : true});
        }
        {
            var Q0;
            Q0=makeQuery(id+"F11.opExtrude","CAP_EDGE",EDGE,{"disambiguationData":[OSD([sQuery(id+"F10.wireOp",EDGE,"E33")])],"isStart":true});
            var Q1;
            Q1=makeQuery(id+"F11.opExtrude","CAP_EDGE",EDGE,{"disambiguationData":[OSD([sQuery(id+"F10.wireOp",EDGE,"E35.MirrorCS")])],"isStart":true});
            var Q2;
            Q2=makeQuery(id+"F11.opExtrude","CAP_EDGE",EDGE,{"disambiguationData":[OSD([sQuery(id+"F10.wireOp",EDGE,"E55.MirrorCS")])],"isStart":true});
            var Q3;
            Q3=makeQuery(id+"F11.opExtrude","CAP_EDGE",EDGE,{"disambiguationData":[OSD([sQuery(id+"F10.wireOp",EDGE,"E54.MirrorCS")])],"isStart":true});
            var Q4;
            Q4=makeQuery(id+"F11.opExtrude","CAP_EDGE",EDGE,{"disambiguationData":[OSD([sQuery(id+"F10.wireOp",EDGE,"E53.bottom")])],"isStart":true});
            var Q5;
            Q5=makeQuery(id+"F11.opExtrude","CAP_EDGE",EDGE,{"disambiguationData":[OSD([sQuery(id+"F10.wireOp",EDGE,"E53.top")])],"isStart":true});
            var Q6;
            Q6=makeQuery(id+"F11.opExtrude","CAP_EDGE",EDGE,{"disambiguationData":[OSD([sQuery(id+"F10.wireOp",EDGE,"E49.MirrorCS")])],"isStart":true});
            var Q7;
            Q7=makeQuery(id+"F11.opExtrude","CAP_EDGE",EDGE,{"disambiguationData":[OSD([sQuery(id+"F10.wireOp",EDGE,"E41.MirrorCS")])],"isStart":true});
            chamfer(context, id + "F13", {"entities" : qUnion([Q0, Q1, Q2, Q3, Q4, Q5, Q6, Q7]), "width" : 8 * mm, "tangentPropagation" : true});
        }
    });
